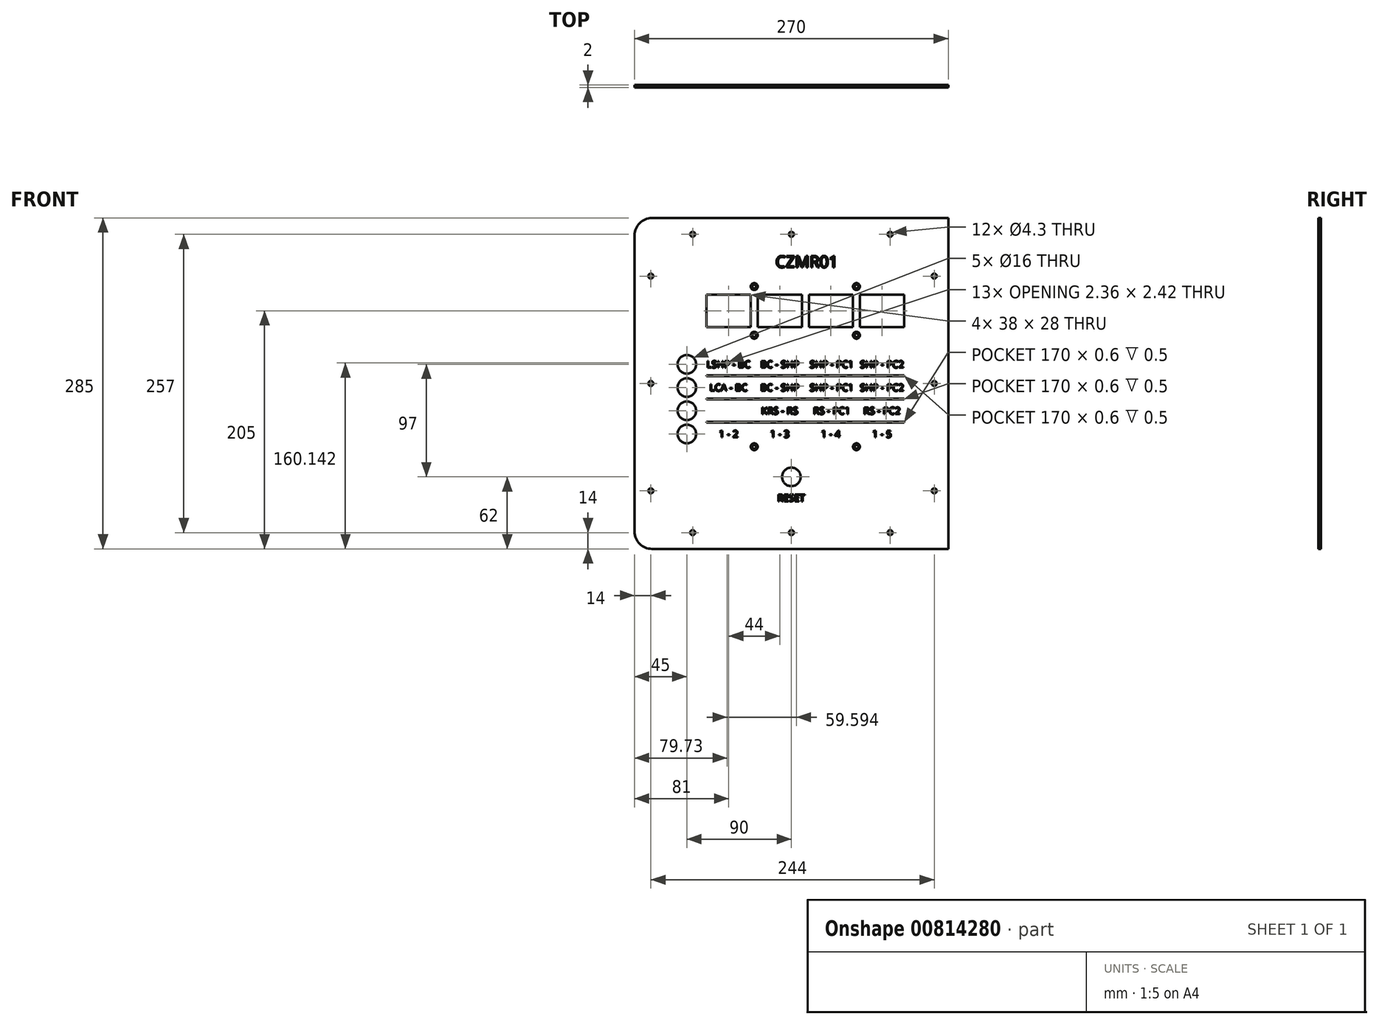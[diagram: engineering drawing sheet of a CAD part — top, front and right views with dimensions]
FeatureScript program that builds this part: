
annotation { "Feature Type Name" : "Feature", "Feature Type Description" : "" }
export const myFeature = defineFeature(function(context is Context, id is Id, definition is map)
    precondition{}
    {
        {
            var Q0;
            Q0=qCreatedBy(makeId("Front.planeOp"),FACE);
            var sketch = newSketch(context, id + "F0", { "sketchPlane" : qUnion([Q0])});
            skLineSegment(sketch, "E0.bottom", {"start": v(-115, 180) * mm, "end": v(155, 180) * mm});
            skLineSegment(sketch, "E0.top", {"start": v(-115, -105) * mm, "end": v(155, -105) * mm});
            skLineSegment(sketch, "E0.left", {"start": v(-115, 180) * mm, "end": v(-115, -105) * mm});
            skLineSegment(sketch, "E0.right", {"start": v(155, 180) * mm, "end": v(155, -105) * mm});
            skLineSegment(sketch, "E1.bottom", {"start": v(0, 0) * mm, "end": v(0, 0) * mm});
            skLineSegment(sketch, "E2.bottom", {"start": v(-15, 114) * mm, "end": v(-53, 114) * mm});
            skLineSegment(sketch, "E2.top", {"start": v(-15, 86) * mm, "end": v(-53, 86) * mm});
            skLineSegment(sketch, "E2.left", {"start": v(-15, 114) * mm, "end": v(-15, 86) * mm});
            skLineSegment(sketch, "E2.right", {"start": v(-53, 114) * mm, "end": v(-53, 86) * mm});
            skPoint(sketch, "E2.middle", {"position": v(-34, 100) * mm});
            skLineSegment(sketch, "E3.bottom", {"start": v(29, 86) * mm, "end": v(-9, 86) * mm});
            skLineSegment(sketch, "E3.top", {"start": v(29, 114) * mm, "end": v(-9, 114) * mm});
            skLineSegment(sketch, "E3.left", {"start": v(29, 86) * mm, "end": v(29, 114) * mm});
            skLineSegment(sketch, "E3.right", {"start": v(-9, 86) * mm, "end": v(-9, 114) * mm});
            skPoint(sketch, "E3.middle", {"position": v(10, 100) * mm});
            skLineSegment(sketch, "E4.bottom", {"start": v(73, 114) * mm, "end": v(35, 114) * mm});
            skLineSegment(sketch, "E4.top", {"start": v(73, 86) * mm, "end": v(35, 86) * mm});
            skLineSegment(sketch, "E4.left", {"start": v(73, 114) * mm, "end": v(73, 86) * mm});
            skLineSegment(sketch, "E4.right", {"start": v(35, 114) * mm, "end": v(35, 86) * mm});
            skPoint(sketch, "E4.middle", {"position": v(54, 100) * mm});
            skLineSegment(sketch, "E5.bottom", {"start": v(79, 114) * mm, "end": v(117, 114) * mm});
            skLineSegment(sketch, "E5.top", {"start": v(79, 86) * mm, "end": v(117, 86) * mm});
            skLineSegment(sketch, "E5.left", {"start": v(79, 114) * mm, "end": v(79, 86) * mm});
            skLineSegment(sketch, "E5.right", {"start": v(117, 114) * mm, "end": v(117, 86) * mm});
            skPoint(sketch, "E5.middle", {"position": v(98, 100) * mm});
            skPoint(sketch, "E6", {"position": v(-12, 121) * mm});
            skPoint(sketch, "E7", {"position": v(-12, 79) * mm});
            skPoint(sketch, "E8", {"position": v(76, 79) * mm});
            skPoint(sketch, "E9", {"position": v(76, 121) * mm});
            skPoint(sketch, "E10", {"position": v(20, -43) * mm});
            skPoint(sketch, "E11", {"position": v(-70, 54) * mm});
            skPoint(sketch, "E12", {"position": v(-70, 34) * mm});
            skPoint(sketch, "E13", {"position": v(-70, 14) * mm});
            skPoint(sketch, "E14", {"position": v(-70, -6) * mm});
            skPoint(sketch, "E15", {"position": v(-101, -55) * mm});
            skPoint(sketch, "E16", {"position": v(-101, 37.5) * mm});
            skPoint(sketch, "E17", {"position": v(-101, 130) * mm});
            skPoint(sketch, "E18", {"position": v(-65, -91) * mm});
            skPoint(sketch, "E19", {"position": v(20, -91) * mm});
            skPoint(sketch, "E20", {"position": v(143, -55) * mm});
            skPoint(sketch, "E21", {"position": v(-65, 166) * mm});
            skPoint(sketch, "E22", {"position": v(20, 166) * mm});
            skPoint(sketch, "E23", {"position": v(143, 130) * mm});
            skPoint(sketch, "E24", {"position": v(143, 37.5) * mm});
            skPoint(sketch, "E25", {"position": v(20, -105) * mm});
            skPoint(sketch, "E26", {"position": v(105, -91) * mm});
            skPoint(sketch, "E27", {"position": v(105, 166) * mm});
            skPoint(sketch, "E28", {"position": v(-115, 37.5) * mm});
            skPoint(sketch, "E29", {"position": v(20, 180) * mm});
            skPoint(sketch, "E30", {"position": v(155, 37.5) * mm});
            skPoint(sketch, "E31", {"position": v(76, -17) * mm});
            skPoint(sketch, "E32", {"position": v(-12, -17) * mm});
            skSolve(sketch);
        }
        {
            var Q0;
            Q0=makeQuery(id+"F0.imprint","IMPRINT",FACE,{"disambiguationData":[TD([[makeQuery(id+"F0.imprint","IMPRINT",EDGE,{"derivedFrom":sQuery(id+"F0.wireOp",EDGE,"E0.bottom")}),-1.0]])]});
            extrude(context, id + "F1", {"entities" : qUnion([Q0]), "depth" : -2 * mm, "offsetDistance" : 25 * mm});
        }
        {
            var Q0;
            Q0=sQuery(id+"F0.wireOp",VERTEX,"91fe99ce-f820-44d3-a060-ec0d8d303532");
            var Q1;
            Q1=sQuery(id+"F0.wireOp",VERTEX,"81f7b9a9-a607-461f-8039-cb821bf447f8");
            var Q2;
            Q2=sQuery(id+"F0.wireOp",VERTEX,"691b8013-0834-4f03-ac6f-debae8ae6253");
            var Q3;
            Q3=sQuery(id+"F0.wireOp",VERTEX,"9db44c55-5db1-4255-af30-b09b77b20d7c");
            var Q4;
            Q4=sQuery(id+"F0.wireOp",VERTEX,"E6");
            var Q5;
            Q5=sQuery(id+"F0.wireOp",VERTEX,"E9");
            var Q6;
            Q6=sQuery(id+"F0.wireOp",VERTEX,"E8");
            var Q7;
            Q7=sQuery(id+"F0.wireOp",VERTEX,"E7");
            var Q8;
            Q8=sQuery(id+"F0.wireOp",VERTEX,"f035614c-013f-41b0-ac28-023a41dd84ef");
            var Q9;
            Q9=sQuery(id+"F0.wireOp",VERTEX,"ed18d827-31f1-407b-bbdd-cd717bbfd4c2");
            var Q10;
            Q10=sQuery(id+"F0.wireOp",VERTEX,"E32");
            var Q11;
            Q11=sQuery(id+"F0.wireOp",VERTEX,"E31");
            var Q12;
            Q12=makeQuery(id+"F1.opExtrude","SWEPT_BODY",BODY,{"disambiguationData":[OSD([sQuery(id+"F0.wireOp",EDGE,"E0.bottom"),sQuery(id+"F0.wireOp",EDGE,"E0.top"),sQuery(id+"F0.wireOp",EDGE,"E0.left"),sQuery(id+"F0.wireOp",EDGE,"E0.right"),sQuery(id+"F0.wireOp",EDGE,"lFYCYkB5-TIvG-fpRE-Ozdr-Ed2Nn7j2ueNT.bottom"),sQuery(id+"F0.wireOp",EDGE,"lFYCYkB5-TIvG-fpRE-Ozdr-Ed2Nn7j2ueNT.top"),sQuery(id+"F0.wireOp",EDGE,"lFYCYkB5-TIvG-fpRE-Ozdr-Ed2Nn7j2ueNT.left"),sQuery(id+"F0.wireOp",EDGE,"lFYCYkB5-TIvG-fpRE-Ozdr-Ed2Nn7j2ueNT.right"),sQuery(id+"F0.wireOp",EDGE,"E2.bottom"),sQuery(id+"F0.wireOp",EDGE,"E2.top"),sQuery(id+"F0.wireOp",EDGE,"E2.left"),sQuery(id+"F0.wireOp",EDGE,"E2.right"),sQuery(id+"F0.wireOp",EDGE,"E3.bottom"),sQuery(id+"F0.wireOp",EDGE,"E3.top"),sQuery(id+"F0.wireOp",EDGE,"E3.left"),sQuery(id+"F0.wireOp",EDGE,"E3.right"),sQuery(id+"F0.wireOp",EDGE,"E4.bottom"),sQuery(id+"F0.wireOp",EDGE,"E4.top"),sQuery(id+"F0.wireOp",EDGE,"E4.left"),sQuery(id+"F0.wireOp",EDGE,"E4.right"),sQuery(id+"F0.wireOp",EDGE,"E5.bottom"),sQuery(id+"F0.wireOp",EDGE,"E5.top"),sQuery(id+"F0.wireOp",EDGE,"E5.left"),sQuery(id+"F0.wireOp",EDGE,"E5.right"),sQuery(id+"F0.wireOp",EDGE,"6LnHnKh7-kymI-xe4V-cifd-BYv3m9t67Dne.bottom"),sQuery(id+"F0.wireOp",EDGE,"6LnHnKh7-kymI-xe4V-cifd-BYv3m9t67Dne.top"),sQuery(id+"F0.wireOp",EDGE,"6LnHnKh7-kymI-xe4V-cifd-BYv3m9t67Dne.left"),sQuery(id+"F0.wireOp",EDGE,"6LnHnKh7-kymI-xe4V-cifd-BYv3m9t67Dne.right"),sQuery(id+"F0.wireOp",EDGE,"ZRxind2v-mckt-qEpB-JpKv-uTAhQe7Ge2PS.bottom"),sQuery(id+"F0.wireOp",EDGE,"ZRxind2v-mckt-qEpB-JpKv-uTAhQe7Ge2PS.top"),sQuery(id+"F0.wireOp",EDGE,"ZRxind2v-mckt-qEpB-JpKv-uTAhQe7Ge2PS.left"),sQuery(id+"F0.wireOp",EDGE,"ZRxind2v-mckt-qEpB-JpKv-uTAhQe7Ge2PS.right"),sQuery(id+"F0.wireOp",EDGE,"YbEPNr4H-6yva-OXlj-h1Es-tT3npC0D80Da.bottom"),sQuery(id+"F0.wireOp",EDGE,"YbEPNr4H-6yva-OXlj-h1Es-tT3npC0D80Da.top"),sQuery(id+"F0.wireOp",EDGE,"YbEPNr4H-6yva-OXlj-h1Es-tT3npC0D80Da.left"),sQuery(id+"F0.wireOp",EDGE,"YbEPNr4H-6yva-OXlj-h1Es-tT3npC0D80Da.right"),sQuery(id+"F0.wireOp",EDGE,"F3dLYiNU-b4QI-GJ9a-ZSmS-QTg4546Lzhh8.bottom"),sQuery(id+"F0.wireOp",EDGE,"F3dLYiNU-b4QI-GJ9a-ZSmS-QTg4546Lzhh8.top"),sQuery(id+"F0.wireOp",EDGE,"F3dLYiNU-b4QI-GJ9a-ZSmS-QTg4546Lzhh8.left"),sQuery(id+"F0.wireOp",EDGE,"F3dLYiNU-b4QI-GJ9a-ZSmS-QTg4546Lzhh8.right")])]});
            hole(context, id + "F2", {"style" : HoleStyle.C_SINK, "endStyle" : HoleEndStyle.THROUGH, "holeDiameter" : 3.2 * mm, "cSinkDiameter" : 6 * mm, "cSinkAngle" : 90 * degree, "majorDiameter" : 5 * mm, "isTappedThrough" : true, "tappedDepth" : 12 * mm, "tapClearance" : 3, "locations" : qUnion([Q0, Q1, Q2, Q3, Q4, Q5, Q6, Q7, Q8, Q9, Q10, Q11]), "scope" : qUnion([Q12]), "startStyle" : HoleStartStyle.SKETCH});
        }
        {
            var Q0;
            Q0=makeQuery(id+"F1.opExtrude","SWEPT_EDGE",EDGE,{"disambiguationData":[OSD([sQuery(id+"F0.wireOp",EDGE,"E0.bottom"),sQuery(id+"F0.wireOp",EDGE,"E0.left")])]});
            var Q1;
            Q1=makeQuery(id+"F1.opExtrude","SWEPT_EDGE",EDGE,{"disambiguationData":[OSD([sQuery(id+"F0.wireOp",EDGE,"E0.top"),sQuery(id+"F0.wireOp",EDGE,"E0.left")])]});
            fillet(context, id + "F3", {"entities" : qUnion([Q0, Q1]), "radius" : 15 * mm, "tangentPropagation" : true, "allowEdgeOverflow" : false});
        }
        {
            var Q0;
            Q0=sQuery(id+"F0.wireOp",VERTEX,"E11");
            var Q1;
            Q1=sQuery(id+"F0.wireOp",VERTEX,"E12");
            var Q2;
            Q2=sQuery(id+"F0.wireOp",VERTEX,"E13");
            var Q3;
            Q3=sQuery(id+"F0.wireOp",VERTEX,"E14");
            var Q4;
            Q4=sQuery(id+"F0.wireOp",VERTEX,"E10");
            var Q5;
            Q5=makeQuery(id+"F1.opExtrude","SWEPT_BODY",BODY,{"disambiguationData":[OSD([sQuery(id+"F0.wireOp",EDGE,"E0.bottom"),sQuery(id+"F0.wireOp",EDGE,"E0.top"),sQuery(id+"F0.wireOp",EDGE,"E0.left"),sQuery(id+"F0.wireOp",EDGE,"E0.right"),sQuery(id+"F0.wireOp",EDGE,"E2.bottom"),sQuery(id+"F0.wireOp",EDGE,"E2.top"),sQuery(id+"F0.wireOp",EDGE,"E2.left"),sQuery(id+"F0.wireOp",EDGE,"E2.right"),sQuery(id+"F0.wireOp",EDGE,"E3.bottom"),sQuery(id+"F0.wireOp",EDGE,"E3.top"),sQuery(id+"F0.wireOp",EDGE,"E3.left"),sQuery(id+"F0.wireOp",EDGE,"E3.right"),sQuery(id+"F0.wireOp",EDGE,"E4.bottom"),sQuery(id+"F0.wireOp",EDGE,"E4.top"),sQuery(id+"F0.wireOp",EDGE,"E4.left"),sQuery(id+"F0.wireOp",EDGE,"E4.right"),sQuery(id+"F0.wireOp",EDGE,"E5.bottom"),sQuery(id+"F0.wireOp",EDGE,"E5.top"),sQuery(id+"F0.wireOp",EDGE,"E5.left"),sQuery(id+"F0.wireOp",EDGE,"E5.right")])]});
            hole(context, id + "F4", {"style" : HoleStyle.SIMPLE, "endStyle" : HoleEndStyle.THROUGH, "holeDiameter" : 16 * mm, "majorDiameter" : 5 * mm, "isTappedThrough" : true, "tappedDepth" : 12 * mm, "tapClearance" : 3, "locations" : qUnion([Q0, Q1, Q2, Q3, Q4]), "scope" : qUnion([Q5]), "startStyle" : HoleStartStyle.SKETCH});
        }
        {
            var Q0;
            Q0=makeQuery(id+"F0.imprint","IMPRINT",FACE,{"disambiguationData":[TD([[makeQuery(id+"F0.imprint","IMPRINT",EDGE,{"derivedFrom":sQuery(id+"F0.wireOp",EDGE,"E0.bottom")}),-1.0]])]});
            var sketch = newSketch(context, id + "F5", { "sketchPlane" : qUnion([Q0]), "disableImprinting" : false});
            skPoint(sketch, "E33.0", {"position": v(-34, 100) * mm});
            skPoint(sketch, "E34.0", {"position": v(10, 100) * mm});
            skPoint(sketch, "E35.0", {"position": v(54, 100) * mm});
            skPoint(sketch, "E36.0", {"position": v(98, 100) * mm});
            skPoint(sketch, "E37.0", {"position": v(20, -43) * mm});
            skText(sketch, "E38", { "text": "LSHP - BC", "fontName": "OpenSans-Regular.ttf"});
            skText(sketch, "E39", { "text": "BC - SHP", "fontName": "OpenSans-Regular.ttf"});
            skPoint(sketch, "E40", {"position": v(-53.01, 54) * mm});
            skText(sketch, "E41", { "text": "SHP - PC1", "fontName": "OpenSans-Regular.ttf"});
            skText(sketch, "E42", { "text": "SHP - PC2", "fontName": "OpenSans-Regular.ttf"});
            skText(sketch, "E43", { "text": "LCA - BC", "fontName": "OpenSans-Regular.ttf"});
            skText(sketch, "E44", { "text": "BC - SHP", "fontName": "OpenSans-Regular.ttf"});
            skText(sketch, "E45", { "text": "SHP - PC1", "fontName": "OpenSans-Regular.ttf"});
            skText(sketch, "E46", { "text": "SHP - PC2", "fontName": "OpenSans-Regular.ttf"});
            skText(sketch, "E47", { "text": "KRS - RS", "fontName": "OpenSans-Regular.ttf"});
            skPoint(sketch, "E48", {"position": v(-5.86, 14) * mm});
            skText(sketch, "E49", { "text": "RS - PC1", "fontName": "OpenSans-Regular.ttf"});
            skText(sketch, "E50", { "text": "RS - PC2", "fontName": "OpenSans-Regular.ttf"});
            skPoint(sketch, "E51.0", {"position": v(-70, 14) * mm});
            skText(sketch, "E52", { "text": "1 - 2", "fontName": "OpenSans-Regular.ttf"});
            skText(sketch, "E53", { "text": "1 - 3", "fontName": "OpenSans-Regular.ttf"});
            skPoint(sketch, "E54", {"position": v(-42.32, -6) * mm});
            skText(sketch, "E55", { "text": "1 - 4", "fontName": "OpenSans-Regular.ttf"});
            skText(sketch, "E56", { "text": "1 - 5", "fontName": "OpenSans-Regular.ttf"});
            skPoint(sketch, "E57.0", {"position": v(-70, -6) * mm});
            skText(sketch, "E58", { "text": "RESET", "fontName": "OpenSans-Regular.ttf"});
            skPoint(sketch, "E59.0", {"position": v(-70, 54) * mm});
            skPoint(sketch, "E60.0", {"position": v(-70, 34) * mm});
            skLineSegment(sketch, "E61", {"start": v(10, 100) * mm, "end": v(54, 100) * mm, "construction": true});
            skLineSegment(sketch, "E62.bottom", {"start": v(116.94, 44.3) * mm, "end": v(-53.06, 44.3) * mm});
            skLineSegment(sketch, "E62.top", {"start": v(116.94, 43.7) * mm, "end": v(-53.06, 43.7) * mm});
            skLineSegment(sketch, "E62.left", {"start": v(116.94, 44.3) * mm, "end": v(116.94, 43.7) * mm});
            skLineSegment(sketch, "E62.right", {"start": v(-53.06, 44.3) * mm, "end": v(-53.06, 43.7) * mm});
            skPoint(sketch, "E62.middle", {"position": v(31.94, 44) * mm});
            skLineSegment(sketch, "E63.bottom", {"start": v(116.94, 3.7) * mm, "end": v(-53.06, 3.7) * mm});
            skLineSegment(sketch, "E63.top", {"start": v(116.94, 4.3) * mm, "end": v(-53.06, 4.3) * mm});
            skLineSegment(sketch, "E63.left", {"start": v(116.94, 3.7) * mm, "end": v(116.94, 4.3) * mm});
            skLineSegment(sketch, "E63.right", {"start": v(-53.06, 3.7) * mm, "end": v(-53.06, 4.3) * mm});
            skPoint(sketch, "E63.middle", {"position": v(31.94, 24) * mm});
            skLineSegment(sketch, "E64.bottom", {"start": v(116.94, 23.7) * mm, "end": v(-53.06, 23.7) * mm});
            skLineSegment(sketch, "E64.top", {"start": v(116.94, 24.3) * mm, "end": v(-53.06, 24.3) * mm});
            skLineSegment(sketch, "E64.left", {"start": v(116.94, 23.7) * mm, "end": v(116.94, 24.3) * mm});
            skLineSegment(sketch, "E64.right", {"start": v(-53.06, 23.7) * mm, "end": v(-53.06, 24.3) * mm});
            skLineSegment(sketch, "E65", {"start": v(-70, 54) * mm, "end": v(-70, 34) * mm, "construction": true});
            skLineSegment(sketch, "E66", {"start": v(-70, 34) * mm, "end": v(-70, 14) * mm, "construction": true});
            skLineSegment(sketch, "E67", {"start": v(-70, 14) * mm, "end": v(-70, -6) * mm, "construction": true});
            skPoint(sketch, "E68", {"position": v(-70, 44) * mm});
            skPoint(sketch, "E69", {"position": v(-70, 24) * mm});
            skPoint(sketch, "E70", {"position": v(-70, 4) * mm});
            skPoint(sketch, "E71", {"position": v(31.94, 4) * mm});
            skText(sketch, "E72", { "text": "CZMR01", "fontName": "OpenSans-Regular.ttf"});
            skPoint(sketch, "E73", {"position": v(32.1, 100) * mm});
            const initialGuessF5  = {"E38": [-0.05301, 0.051, 1, 0, 0.006], "E39": [-0.00676, 0.051, 1, 0, 0.006], "E41": [0.03576, 0.051, 1, 0, 0.006], "E42": [0.07906, 0.051, 1, 0, 0.006], "E43": [-0.0504, 0.031, 1, 0, 0.006], "E44": [-0.00676, 0.031, 1, 0, 0.006], "E45": [0.03576, 0.031, 1, 0, 0.006], "E46": [0.07906, 0.031, 1, 0, 0.006], "E47": [-0.00586, 0.011, 1, 0, 0.006], "E49": [0.03877, 0.011, 1, 0, 0.006], "E50": [0.08207, 0.011, 1, 0, 0.006], "E52": [-0.04232, -0.009, 1, 0, 0.006], "E53": [0.0017, -0.009, 1, 0, 0.006], "E55": [0.04554, -0.009, 1, 0, 0.006], "E56": [0.0897, -0.009, 1, 0, 0.006], "E58": [0.00797, -0.064, 1, 0, 0.006], "E72": [0.00634, 0.13741, 1, 0, 0.01]};
            skSetInitialGuess(sketch, initialGuessF5);
            skSolve(sketch);
        }
        {
            var Q0;
            Q0 = qSketchRegion(id + "F5", true);
            extrude(context, id + "F6", {"entities" : qUnion([Q0]), "operationType" : NewBodyOperationType.REMOVE, "oppositeDirection" : true, "depth" : 0.5 * mm, "offsetDistance" : 25 * mm});
        }
        {
            var Q0;
            Q0=sQuery(id+"F0.wireOp",VERTEX,"E17");
            var Q1;
            Q1=sQuery(id+"F0.wireOp",VERTEX,"E21");
            var Q2;
            Q2=sQuery(id+"F0.wireOp",VERTEX,"E22");
            var Q3;
            Q3=sQuery(id+"F0.wireOp",VERTEX,"E23");
            var Q4;
            Q4=sQuery(id+"F0.wireOp",VERTEX,"9d722ff5-f00b-40e0-acfb-ca4bb0152902");
            var Q5;
            Q5=sQuery(id+"F0.wireOp",VERTEX,"c1d490f0-b6d4-4fe4-9a08-d95329df1111");
            var Q6;
            Q6=sQuery(id+"F0.wireOp",VERTEX,"E16");
            var Q7;
            Q7=sQuery(id+"F0.wireOp",VERTEX,"E24");
            var Q8;
            Q8=sQuery(id+"F0.wireOp",VERTEX,"E15");
            var Q9;
            Q9=sQuery(id+"F0.wireOp",VERTEX,"E18");
            var Q10;
            Q10=sQuery(id+"F0.wireOp",VERTEX,"E19");
            var Q11;
            Q11=sQuery(id+"F0.wireOp",VERTEX,"E20");
            var Q12;
            Q12=sQuery(id+"F0.wireOp",VERTEX,"E27");
            var Q13;
            Q13=sQuery(id+"F0.wireOp",VERTEX,"E26");
            var Q14;
            Q14=makeQuery(id+"F1.opExtrude","SWEPT_BODY",BODY,{"disambiguationData":[OSD([sQuery(id+"F0.wireOp",EDGE,"E0.bottom"),sQuery(id+"F0.wireOp",EDGE,"E0.top"),sQuery(id+"F0.wireOp",EDGE,"E0.left"),sQuery(id+"F0.wireOp",EDGE,"E0.right"),sQuery(id+"F0.wireOp",EDGE,"E2.bottom"),sQuery(id+"F0.wireOp",EDGE,"E2.top"),sQuery(id+"F0.wireOp",EDGE,"E2.left"),sQuery(id+"F0.wireOp",EDGE,"E2.right"),sQuery(id+"F0.wireOp",EDGE,"E3.bottom"),sQuery(id+"F0.wireOp",EDGE,"E3.top"),sQuery(id+"F0.wireOp",EDGE,"E3.left"),sQuery(id+"F0.wireOp",EDGE,"E3.right"),sQuery(id+"F0.wireOp",EDGE,"E4.bottom"),sQuery(id+"F0.wireOp",EDGE,"E4.top"),sQuery(id+"F0.wireOp",EDGE,"E4.left"),sQuery(id+"F0.wireOp",EDGE,"E4.right"),sQuery(id+"F0.wireOp",EDGE,"E5.bottom"),sQuery(id+"F0.wireOp",EDGE,"E5.top"),sQuery(id+"F0.wireOp",EDGE,"E5.left"),sQuery(id+"F0.wireOp",EDGE,"E5.right")])]});
            hole(context, id + "F7", {"style" : HoleStyle.SIMPLE, "endStyle" : HoleEndStyle.THROUGH, "holeDiameter" : 4.3 * mm, "majorDiameter" : 5 * mm, "isTappedThrough" : true, "tappedDepth" : 12 * mm, "tapClearance" : 3, "locations" : qUnion([Q0, Q1, Q2, Q3, Q4, Q5, Q6, Q7, Q8, Q9, Q10, Q11, Q12, Q13]), "scope" : qUnion([Q14]), "startStyle" : HoleStartStyle.SKETCH});
        }
        {
            var Q0;
            Q0 = qSketchRegion(id + "F5", true);
            extrude(context, id + "F8", {"entities" : qUnion([Q0]), "domain" : OperationDomain.MODEL, "flatOperationType" : FlatOperationType.REMOVE, "oppositeDirection" : true, "depth" : 1 * mm, "offsetDistance" : 25 * mm, "startOffsetBound" : StartOffsetType.BLIND, "startOffsetDistance" : 25 * mm});
        }
    });
